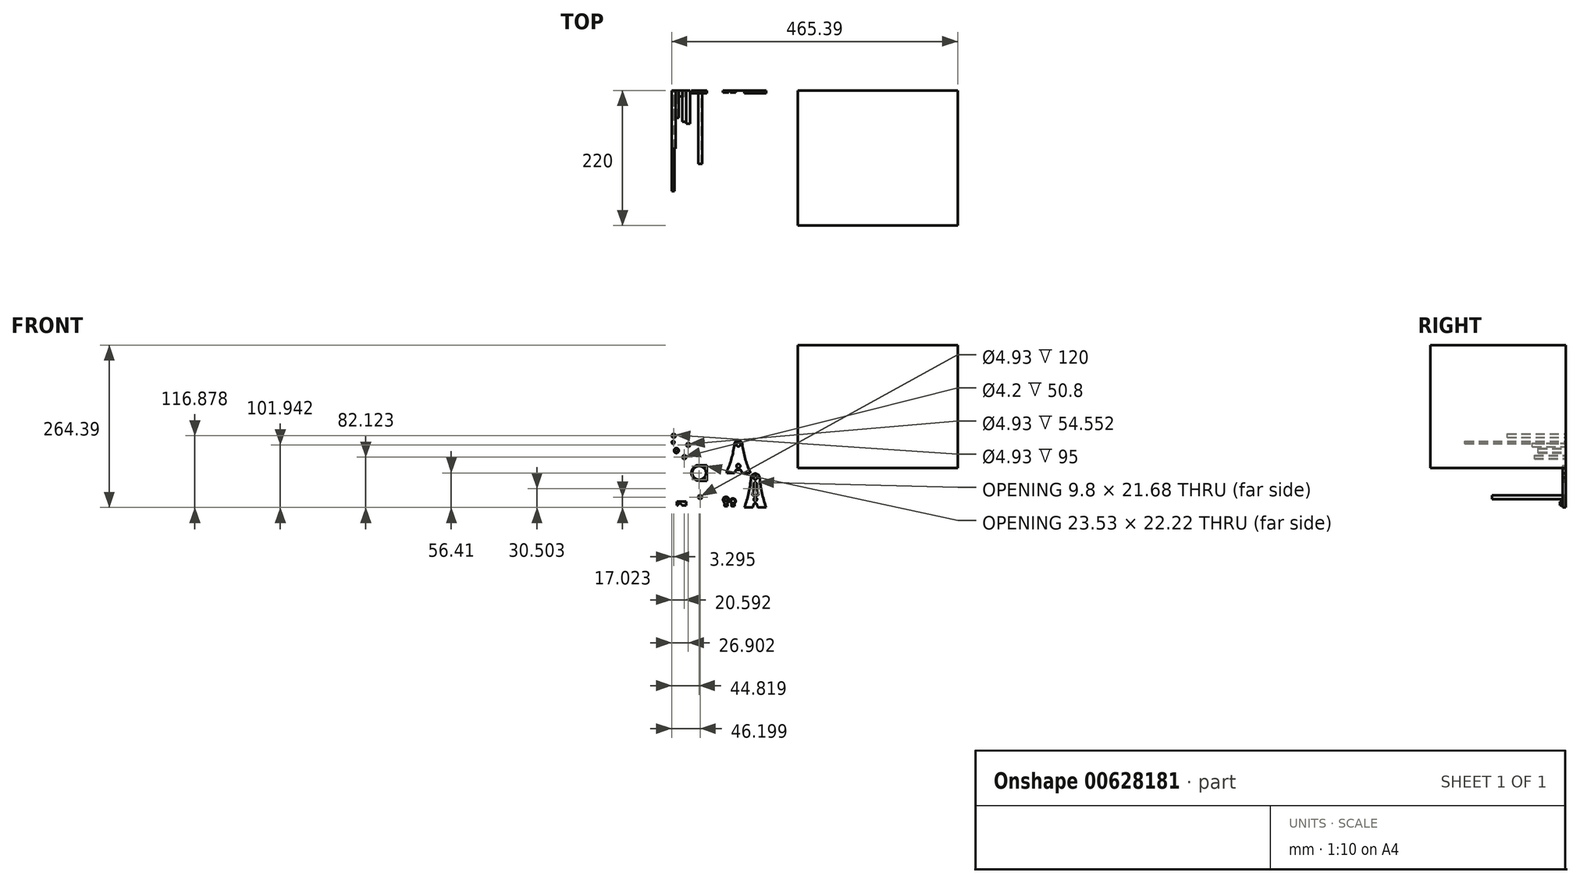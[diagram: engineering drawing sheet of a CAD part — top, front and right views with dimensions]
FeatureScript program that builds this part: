
annotation { "Feature Type Name" : "Feature", "Feature Type Description" : "" }
export const myFeature = defineFeature(function(context is Context, id is Id, definition is map)
    precondition{}
    {
        {
            var Q0;
            Q0=qCreatedBy(makeId("Front.planeOp"),FACE);
            var sketch = newSketch(context, id + "F0", { "sketchPlane" : qUnion([Q0])});
            skLineSegment(sketch, "E0", {"start": v(35.24, 47.42) * mm, "end": v(35.24, 0) * mm, "construction": true});
            skLineSegment(sketch, "E1", {"start": v(16.19, 0) * mm, "end": v(28.89, 0) * mm});
            skCircle(sketch, "E2", {"center": v(35.24, 46.26) * mm, "radius": 3.18 * mm});
            skArc(sketch, "E3", {"start": v(41.73, 46.58) * mm, "mid": v(35.24, 52.76) * mm, "end": v(28.75, 46.58) * mm});
            skLineSegment(sketch, "E4", {"start": v(27.67, 28.76) * mm, "end": v(44.56, 28.76) * mm, "construction": true});
            skCircle(sketch, "E5.MirrorC", {"center": v(35.24, 11.26) * mm, "radius": 3.18 * mm});
            skArc(sketch, "E6.MirrorC", {"start": v(29.85, 7.62) * mm, "mid": v(36.53, 17.63) * mm, "end": v(38.78, 5.81) * mm, "construction": true});
            skLineSegment(sketch, "E7.MirrorCS", {"start": v(54.29, 0) * mm, "end": v(41.59, 0) * mm});
            skPoint(sketch, "E8.orphan", {"position": v(35.24, 0) * mm});
            skArc(sketch, "E9", {"start": v(37.6, 5.2) * mm, "mid": v(33.59, 4.98) * mm, "end": v(30.21, 7.14) * mm});
            skArc(sketch, "E10.trimOffspring", {"start": v(37.92, 5.34) * mm, "mid": v(34.3, 4.83) * mm, "end": v(31, 6.34) * mm, "construction": true});
            skPoint(sketch, "E11.visualSharp", {"position": v(30.21, 7.14) * mm});
            skPoint(sketch, "E12.visualSharp", {"position": v(38.71, 5.77) * mm});
            skLineSegment(sketch, "E13", {"start": v(41.59, 0) * mm, "end": v(39.52, 4.43) * mm});
            skArc(sketch, "E14.filletArc", {"start": v(39.52, 4.43) * mm, "mid": v(38.71, 5.2) * mm, "end": v(37.6, 5.2) * mm});
            skArc(sketch, "E15.MirrorCS", {"start": v(30.95, 4.43) * mm, "mid": v(31.77, 5.2) * mm, "end": v(32.89, 5.2) * mm});
            skLineSegment(sketch, "E16.MirrorCS", {"start": v(28.89, 0) * mm, "end": v(30.95, 4.43) * mm});
            skArc(sketch, "E17", {"start": v(35.17, 39.95) * mm, "mid": v(35.24, 39.95) * mm, "end": v(35.3, 39.95) * mm});
            skArc(sketch, "E18", {"start": v(33.18, 18.44) * mm, "mid": v(35.24, 17.76) * mm, "end": v(37.3, 18.44) * mm});
            skPoint(sketch, "E19.orphan", {"position": v(42.82, 7.9) * mm});
            skPoint(sketch, "E20.orphan", {"position": v(27.65, 7.9) * mm});
            skPoint(sketch, "E21.orphan", {"position": v(35.94, 39.83) * mm});
            skPoint(sketch, "E22.orphan", {"position": v(34.54, 39.83) * mm});
            skPoint(sketch, "E23.visualSharp", {"position": v(31.8, 21.04) * mm});
            skArc(sketch, "E23.filletArc", {"start": v(32.02, 21.82) * mm, "mid": v(32.08, 19.95) * mm, "end": v(33.18, 18.44) * mm});
            skPoint(sketch, "E24.visualSharp", {"position": v(38.68, 21.04) * mm});
            skArc(sketch, "E24.filletArc", {"start": v(37.3, 18.44) * mm, "mid": v(38.4, 19.95) * mm, "end": v(38.46, 21.82) * mm});
            skLineSegment(sketch, "E25", {"start": v(16.19, 0) * mm, "end": v(16.19, 1.6) * mm});
            skArc(sketch, "E26", {"start": v(34.99, 37.23) * mm, "mid": v(35.24, 37.2) * mm, "end": v(35.5, 37.23) * mm});
            skPoint(sketch, "E26.first.point", {"position": v(35.24, 39.95) * mm});
            skArc(sketch, "E27.MirrorCS", {"start": v(54.29, 1.6) * mm, "mid": v(46.28, 23.6) * mm, "end": v(41.73, 46.58) * mm});
            skLineSegment(sketch, "E28.MirrorCS", {"start": v(54.29, 0) * mm, "end": v(54.29, 1.6) * mm});
            skLineSegment(sketch, "E29", {"start": v(28.75, 46.58) * mm, "end": v(28.75, 46.45) * mm});
            skArc(sketch, "E30", {"start": v(16.19, 1.6) * mm, "mid": v(24.2, 23.54) * mm, "end": v(28.75, 46.45) * mm});
            skSolve(sketch);
        }
        {
            var Q0;
            Q0=makeQuery(id+"F0.imprint","IMPRINT",FACE,{"disambiguationData":[TD([[makeQuery(id+"F0.imprint","IMPRINT",EDGE,{"derivedFrom":sQuery(id+"F0.wireOp",EDGE,"E1")}),1.0]])]});
            extrude(context, id + "F1", {"entities" : qUnion([Q0]), "depth" : 3 / 406.4 * mm});
        }
        {
            var Q0;
            Q0=qCreatedBy(makeId("Front.planeOp"),FACE);
            var sketch = newSketch(context, id + "F2", { "sketchPlane" : qUnion([Q0])});
            skCircle(sketch, "E31", {"center": v(-27.02, -39.39) * mm, "radius": 3.18 * mm});
            skCircle(sketch, "E32", {"center": v(-27.02, -39.39) * mm, "radius": 2.46 * mm});
            skSolve(sketch);
        }
        {
            var Q0;
            Q0=makeQuery(id+"F2.imprint","IMPRINT",FACE,{"disambiguationData":[TD([[makeQuery(id+"F2.imprint","IMPRINT",EDGE,{"derivedFrom":sQuery(id+"F2.wireOp",EDGE,"E31")}),1.0]])]});
            extrude(context, id + "F3", {"entities" : qUnion([Q0]), "depth" : 120 * mm});
        }
        {
            var Q0;
            Q0=qCreatedBy(makeId("Front.planeOp"),FACE);
            var sketch = newSketch(context, id + "F4", { "sketchPlane" : qUnion([Q0])});
            skLineSegment(sketch, "E33", {"start": v(12.66, -54.03) * mm, "end": v(12.66, -50.33) * mm});
            skLineSegment(sketch, "E34", {"start": v(17.38, -54.03) * mm, "end": v(17.38, -50.33) * mm});
            skLineSegment(sketch, "E35", {"start": v(12.66, -54.03) * mm, "end": v(17.38, -54.03) * mm});
            skLineSegment(sketch, "E36", {"start": v(17.38, -49.3) * mm, "end": v(18.1, -49.3) * mm});
            skLineSegment(sketch, "E37", {"start": v(18.1, -49.3) * mm, "end": v(18.1, -48.95) * mm});
            skLineSegment(sketch, "E38", {"start": v(15.02, -54.03) * mm, "end": v(15.02, -39.64) * mm, "construction": true});
            skLineSegment(sketch, "E39.MirrorCS", {"start": v(11.94, -49.3) * mm, "end": v(11.94, -48.95) * mm});
            skLineSegment(sketch, "E40.MirrorCS", {"start": v(12.66, -49.3) * mm, "end": v(11.94, -49.3) * mm});
            skLineSegment(sketch, "E41", {"start": v(11.94, -48.3) * mm, "end": v(18.1, -48.3) * mm, "construction": true});
            skArc(sketch, "E42", {"start": v(18.94, -46.24) * mm, "mid": v(15.02, -38.77) * mm, "end": v(11.1, -46.24) * mm});
            skCircle(sketch, "E43", {"center": v(15.02, -43.53) * mm, "radius": 2.5 * mm});
            skArc(sketch, "E44", {"start": v(18.94, -46.24) * mm, "mid": v(19.56, -44.95) * mm, "end": v(19.78, -43.53) * mm, "construction": true});
            skArc(sketch, "E45.filletArc", {"start": v(18.94, -46.24) * mm, "mid": v(18.3, -47.53) * mm, "end": v(18.1, -48.95) * mm});
            skArc(sketch, "E46.MirrorCS", {"start": v(11.1, -46.24) * mm, "mid": v(11.73, -47.53) * mm, "end": v(11.94, -48.95) * mm});
            skArc(sketch, "E47", {"start": v(11.1, -46.24) * mm, "mid": v(15.02, -48.3) * mm, "end": v(18.94, -46.24) * mm, "construction": true});
            skArc(sketch, "E48", {"start": v(17.38, -49.3) * mm, "mid": v(16.87, -49.82) * mm, "end": v(17.38, -50.33) * mm});
            skPoint(sketch, "E49.MirrorCS.start.orphan", {"position": v(18.1, -48.3) * mm});
            skPoint(sketch, "E50.MirrorCS.start.orphan", {"position": v(11.94, -48.3) * mm});
            skArc(sketch, "E51.MirrorCS", {"start": v(12.66, -49.3) * mm, "mid": v(13.16, -49.82) * mm, "end": v(12.66, -50.33) * mm});
            skPoint(sketch, "E52.orphan", {"position": v(12.66, -49.3) * mm});
            skSolve(sketch);
        }
        {
            var Q0;
            Q0=makeQuery(id+"F4.imprint","IMPRINT",FACE,{"disambiguationData":[TD([[makeQuery(id+"F4.imprint","IMPRINT",EDGE,{"derivedFrom":sQuery(id+"F4.wireOp",EDGE,"E33")}),-1.0]])]});
            extrude(context, id + "F5", {"entities" : qUnion([Q0]), "depth" : 3.17 * mm});
        }
        {
            var Q0;
            Q0=makeQuery(id+"F5.opExtrude","SWEPT_FACE",FACE,{"disambiguationData":[OSD([sQuery(id+"F4.wireOp",EDGE,"E35")])]});
            var sketch = newSketch(context, id + "F6", { "sketchPlane" : qUnion([Q0])});
            skLineSegment(sketch, "E53", {"start": v(15.02, 3.18) * mm, "end": v(15.02, 0) * mm, "construction": true});
            skLineSegment(sketch, "E54", {"start": v(12.66, 1.59) * mm, "end": v(17.38, 1.59) * mm, "construction": true});
            skCircle(sketch, "E55", {"center": v(15.02, 1.59) * mm, "radius": 2.37 * mm});
            skSolve(sketch);
        }
        {
            var Q0;
            {var subQ0=sQuery(id+"F6.wireOp",EDGE,"E55");var subQ1=sQuery(id+"F4.wireOp",EDGE,"E35");var subQ2=makeQuery(id+"F5.opExtrude","CAP_EDGE",EDGE,{"disambiguationData":[OSD([subQ1])],"isStart":false});var subQ3=makeQuery(id+"F6.imprint","INTERSECT",VERTEX,{"disambiguationData":[OD(1.0)],"derivedFrom":[subQ2,subQ0]});Q0=makeQuery(id+"F6.imprint","IMPRINT",FACE,{"disambiguationData":[TD([[makeQuery(id+"F6.imprint","IMPRINT",EDGE,{"disambiguationData":[TD([[subQ3,-1.0]])],"derivedFrom":subQ0}),-1.0]])]});}
            var Q1;
            {var subQ0=sQuery(id+"F6.wireOp",EDGE,"E55");var subQ1=sQuery(id+"F4.wireOp",EDGE,"E35");var subQ2=makeQuery(id+"F5.opExtrude","CAP_EDGE",EDGE,{"disambiguationData":[OSD([subQ1])],"isStart":false});var subQ3=makeQuery(id+"F6.imprint","INTERSECT",VERTEX,{"disambiguationData":[OD(0.0)],"derivedFrom":[subQ2,subQ0]});Q1=makeQuery(id+"F6.imprint","IMPRINT",FACE,{"disambiguationData":[TD([[makeQuery(id+"F6.imprint","IMPRINT",EDGE,{"disambiguationData":[TD([[subQ3,1.0]])],"derivedFrom":subQ0}),-1.0]])]});}
            var Q2;
            {var subQ0=sQuery(id+"F6.wireOp",EDGE,"E55");var subQ1=sQuery(id+"F4.wireOp",EDGE,"E35");var subQ4=makeQuery(id+"F5.opExtrude","CAP_EDGE",EDGE,{"disambiguationData":[OSD([subQ1])],"isStart":true});var subQ5=makeQuery(id+"F6.imprint","INTERSECT",VERTEX,{"disambiguationData":[OD(1.0)],"derivedFrom":[subQ4,subQ0]});Q2=makeQuery(id+"F6.imprint","IMPRINT",FACE,{"disambiguationData":[TD([[makeQuery(id+"F6.imprint","IMPRINT",EDGE,{"disambiguationData":[TD([[subQ5,-1.0]])],"derivedFrom":subQ0}),-1.0]])]});}
            var Q3;
            {var subQ0=sQuery(id+"F6.wireOp",EDGE,"E55");var subQ1=sQuery(id+"F4.wireOp",EDGE,"E35");var subQ4=makeQuery(id+"F5.opExtrude","CAP_EDGE",EDGE,{"disambiguationData":[OSD([subQ1])],"isStart":true});var subQ5=makeQuery(id+"F6.imprint","INTERSECT",VERTEX,{"disambiguationData":[OD(0.0)],"derivedFrom":[subQ4,subQ0]});Q3=makeQuery(id+"F6.imprint","IMPRINT",FACE,{"disambiguationData":[TD([[makeQuery(id+"F6.imprint","IMPRINT",EDGE,{"disambiguationData":[TD([[subQ5,1.0]])],"derivedFrom":subQ0}),-1.0]])]});}
            var Q4;
            Q4=sQuery(id+"F6.wireOp",EDGE,"E55");
            var Q5;
            Q5=makeQuery(id+"F5.opExtrude","SWEPT_FACE",FACE,{"disambiguationData":[OSD([sQuery(id+"F4.wireOp",EDGE,"E40.MirrorCS")])]});
            extrude(context, id + "F7", {"entities" : qUnion([Q0, Q1, Q2, Q3]), "operationType" : NewBodyOperationType.REMOVE, "surfaceEntities" : qUnion([Q4]), "endBound" : BoundingType.UP_TO_SURFACE, "oppositeDirection" : true, "endBoundEntityFace" : qUnion([Q5]), "depth" : 25.4 * mm});
        }
        {
            var Q0;
            Q0=qCreatedBy(makeId("Front.planeOp"),FACE);
            var sketch = newSketch(context, id + "F8", { "sketchPlane" : qUnion([Q0])});
            skLineSegment(sketch, "E56", {"start": v(24.01, -54.08) * mm, "end": v(28.94, -54.08) * mm});
            skLineSegment(sketch, "E57", {"start": v(28.94, -54.08) * mm, "end": v(28.94, -50.16) * mm});
            skLineSegment(sketch, "E58", {"start": v(24.01, -54.08) * mm, "end": v(24.01, -50.16) * mm});
            skArc(sketch, "E59", {"start": v(28.94, -49.15) * mm, "mid": v(28.43, -49.66) * mm, "end": v(28.94, -50.16) * mm});
            skLineSegment(sketch, "E60", {"start": v(26.48, -54.08) * mm, "end": v(26.48, -44.7) * mm, "construction": true});
            skLineSegment(sketch, "E61", {"start": v(28.94, -49.15) * mm, "end": v(29.65, -49.15) * mm});
            skLineSegment(sketch, "E62", {"start": v(28.94, -49.15) * mm, "end": v(26.48, -49.15) * mm, "construction": true});
            skArc(sketch, "E63.MirrorCS", {"start": v(24.01, -49.15) * mm, "mid": v(24.52, -49.66) * mm, "end": v(24.01, -50.16) * mm});
            skLineSegment(sketch, "E64.MirrorCS", {"start": v(24.01, -49.15) * mm, "end": v(23.3, -49.15) * mm});
            skCircle(sketch, "E65", {"center": v(26.48, -45.97) * mm, "radius": 3.18 * mm});
            skArc(sketch, "E66", {"start": v(29.65, -49.15) * mm, "mid": v(26.48, -41.48) * mm, "end": v(23.3, -49.15) * mm});
            skSolve(sketch);
        }
        {
            var Q0;
            Q0=makeQuery(id+"F8.imprint","IMPRINT",FACE,{"disambiguationData":[TD([[makeQuery(id+"F8.imprint","IMPRINT",EDGE,{"derivedFrom":sQuery(id+"F8.wireOp",EDGE,"E56")}),1.0]])]});
            extrude(context, id + "F9", {"entities" : qUnion([Q0]), "depth" : 3.17 * mm});
        }
        {
            var Q0;
            Q0=makeQuery(id+"F9.opExtrude","SWEPT_FACE",FACE,{"disambiguationData":[OSD([sQuery(id+"F8.wireOp",EDGE,"E56")])]});
            var sketch = newSketch(context, id + "F10", { "sketchPlane" : qUnion([Q0])});
            skLineSegment(sketch, "E67", {"start": v(28.94, 1.59) * mm, "end": v(24.01, 1.59) * mm, "construction": true});
            skLineSegment(sketch, "E68", {"start": v(26.48, 3.01) * mm, "end": v(26.48, 0) * mm, "construction": true});
            skPoint(sketch, "E68.startSnap0", {"position": v(26.48, 3.18) * mm});
            skCircle(sketch, "E69", {"center": v(26.48, 1.59) * mm, "radius": 2.46 * mm});
            skSolve(sketch);
        }
        {
            var Q0;
            {var subQ0=sQuery(id+"F10.wireOp",EDGE,"E69");var subQ1=sQuery(id+"F8.wireOp",EDGE,"E56");var subQ2=makeQuery(id+"F9.opExtrude","CAP_EDGE",EDGE,{"disambiguationData":[OSD([subQ1])],"isStart":false});var subQ3=makeQuery(id+"F10.imprint","INTERSECT",VERTEX,{"disambiguationData":[OD(1.0)],"derivedFrom":[subQ2,subQ0]});Q0=makeQuery(id+"F10.imprint","IMPRINT",FACE,{"disambiguationData":[TD([[makeQuery(id+"F10.imprint","IMPRINT",EDGE,{"disambiguationData":[TD([[subQ3,-1.0]])],"derivedFrom":subQ0}),-1.0]])]});}
            var Q1;
            {var subQ0=sQuery(id+"F10.wireOp",EDGE,"E69");var subQ1=sQuery(id+"F8.wireOp",EDGE,"E56");var subQ2=makeQuery(id+"F9.opExtrude","CAP_EDGE",EDGE,{"disambiguationData":[OSD([subQ1])],"isStart":false});var subQ3=makeQuery(id+"F10.imprint","INTERSECT",VERTEX,{"disambiguationData":[OD(0.0)],"derivedFrom":[subQ2,subQ0]});Q1=makeQuery(id+"F10.imprint","IMPRINT",FACE,{"disambiguationData":[TD([[makeQuery(id+"F10.imprint","IMPRINT",EDGE,{"disambiguationData":[TD([[subQ3,1.0]])],"derivedFrom":subQ0}),-1.0]])]});}
            var Q2;
            {var subQ0=sQuery(id+"F10.wireOp",EDGE,"E69");var subQ1=sQuery(id+"F8.wireOp",EDGE,"E56");var subQ4=makeQuery(id+"F9.opExtrude","CAP_EDGE",EDGE,{"disambiguationData":[OSD([subQ1])],"isStart":true});var subQ5=makeQuery(id+"F10.imprint","INTERSECT",VERTEX,{"disambiguationData":[OD(0.0)],"derivedFrom":[subQ4,subQ0]});Q2=makeQuery(id+"F10.imprint","IMPRINT",FACE,{"disambiguationData":[TD([[makeQuery(id+"F10.imprint","IMPRINT",EDGE,{"disambiguationData":[TD([[subQ5,1.0]])],"derivedFrom":subQ0}),-1.0]])]});}
            var Q3;
            {var subQ0=sQuery(id+"F10.wireOp",EDGE,"E69");var subQ1=sQuery(id+"F8.wireOp",EDGE,"E56");var subQ4=makeQuery(id+"F9.opExtrude","CAP_EDGE",EDGE,{"disambiguationData":[OSD([subQ1])],"isStart":true});var subQ5=makeQuery(id+"F10.imprint","INTERSECT",VERTEX,{"disambiguationData":[OD(1.0)],"derivedFrom":[subQ4,subQ0]});Q3=makeQuery(id+"F10.imprint","IMPRINT",FACE,{"disambiguationData":[TD([[makeQuery(id+"F10.imprint","IMPRINT",EDGE,{"disambiguationData":[TD([[subQ5,-1.0]])],"derivedFrom":subQ0}),-1.0]])]});}
            var Q4;
            Q4=makeQuery(id+"F9.opExtrude","SWEPT_FACE",FACE,{"disambiguationData":[OSD([sQuery(id+"F8.wireOp",EDGE,"E64.MirrorCS")])]});
            extrude(context, id + "F11", {"entities" : qUnion([Q0, Q1, Q2, Q3]), "operationType" : NewBodyOperationType.REMOVE, "endBound" : BoundingType.UP_TO_SURFACE, "oppositeDirection" : true, "endBoundEntityFace" : qUnion([Q4]), "depth" : 25.4 * mm});
        }
        {
            var Q0;
            Q0=qCreatedBy(makeId("Front.planeOp"),FACE);
            var sketch = newSketch(context, id + "F12", { "sketchPlane" : qUnion([Q0])});
            skLineSegment(sketch, "E70", {"start": v(45.19, -56.41) * mm, "end": v(58.6, -56.41) * mm});
            skLineSegment(sketch, "E71", {"start": v(62.84, -56.41) * mm, "end": v(62.84, 31.77) * mm, "construction": true});
            skCircle(sketch, "E72", {"center": v(62.84, -43.06) * mm, "radius": 7 * mm, "construction": true});
            skCircle(sketch, "E73", {"center": v(62.84, -43.06) * mm, "radius": 2.87 * mm});
            skCircle(sketch, "E74", {"center": v(62.84, -8.06) * mm, "radius": 7 * mm, "construction": true});
            skCircle(sketch, "E75", {"center": v(62.84, -8.06) * mm, "radius": 2.87 * mm});
            skLineSegment(sketch, "E76", {"start": v(62.84, -8.06) * mm, "end": v(55.84, -8.06) * mm, "construction": true});
            skArc(sketch, "E77", {"start": v(45.19, -56.41) * mm, "mid": v(52, -32.57) * mm, "end": v(55.84, -8.06) * mm});
            skArc(sketch, "E78", {"start": v(69.84, -8.06) * mm, "mid": v(62.84, -1.06) * mm, "end": v(55.84, -8.06) * mm});
            skArc(sketch, "E79.0", {"start": v(57.98, -34.9) * mm, "mid": v(59.84, -25.68) * mm, "end": v(61.28, -16.39) * mm});
            skArc(sketch, "E80.0", {"start": v(58.6, -56.41) * mm, "mid": v(59.46, -53.75) * mm, "end": v(60.29, -51.08) * mm});
            skArc(sketch, "E81", {"start": v(62.8, -15.06) * mm, "mid": v(62.82, -15.06) * mm, "end": v(62.84, -15.06) * mm});
            skArc(sketch, "E82", {"start": v(60.07, -36.64) * mm, "mid": v(61.43, -36.2) * mm, "end": v(62.84, -36.06) * mm});
            skArc(sketch, "E83", {"start": v(61.94, -50) * mm, "mid": v(62.4, -50.05) * mm, "end": v(62.84, -50.06) * mm});
            skPoint(sketch, "E84.visualSharp", {"position": v(56.94, -39.3) * mm});
            skArc(sketch, "E84.filletArc", {"start": v(57.98, -34.9) * mm, "mid": v(58.5, -36.41) * mm, "end": v(60.07, -36.64) * mm});
            skPoint(sketch, "E85.visualSharp", {"position": v(60.7, -49.73) * mm});
            skArc(sketch, "E85.filletArc", {"start": v(61.94, -50) * mm, "mid": v(60.92, -50.24) * mm, "end": v(60.29, -51.08) * mm});
            skPoint(sketch, "E86.visualSharp", {"position": v(61.47, -14.93) * mm});
            skArc(sketch, "E86.filletArc", {"start": v(62.8, -15.06) * mm, "mid": v(61.8, -15.44) * mm, "end": v(61.28, -16.39) * mm});
            skArc(sketch, "E87.MirrorCS", {"start": v(67.7, -34.9) * mm, "mid": v(65.84, -25.68) * mm, "end": v(64.4, -16.39) * mm});
            skPoint(sketch, "E88.MirrorP", {"position": v(64.21, -14.93) * mm});
            skArc(sketch, "E89.MirrorCS", {"start": v(62.88, -15.06) * mm, "mid": v(63.89, -15.44) * mm, "end": v(64.4, -16.39) * mm});
            skArc(sketch, "E90.MirrorCS", {"start": v(67.7, -34.9) * mm, "mid": v(67.2, -36.41) * mm, "end": v(65.62, -36.64) * mm});
            skArc(sketch, "E91.MirrorCS", {"start": v(63.74, -50) * mm, "mid": v(64.76, -50.24) * mm, "end": v(65.4, -51.08) * mm});
            skArc(sketch, "E92.MirrorCS", {"start": v(67.08, -56.41) * mm, "mid": v(66.22, -53.75) * mm, "end": v(65.4, -51.08) * mm});
            skLineSegment(sketch, "E93.MirrorCS", {"start": v(80.5, -56.41) * mm, "end": v(67.08, -56.41) * mm});
            skArc(sketch, "E94.MirrorCS", {"start": v(80.5, -56.41) * mm, "mid": v(73.7, -32.57) * mm, "end": v(69.84, -8.06) * mm});
            skPoint(sketch, "E95.orphan", {"position": v(62.84, -56.41) * mm});
            skArc(sketch, "E96", {"start": v(62.84, -36.06) * mm, "mid": v(64.26, -36.2) * mm, "end": v(65.62, -36.64) * mm});
            skArc(sketch, "E97", {"start": v(62.84, -50.06) * mm, "mid": v(63.3, -50.05) * mm, "end": v(63.74, -50) * mm});
            skArc(sketch, "E98.MirrorCS", {"start": v(62.88, -15.06) * mm, "mid": v(62.86, -15.06) * mm, "end": v(62.84, -15.06) * mm});
            skSolve(sketch);
        }
        {
            var Q0;
            Q0=makeQuery(id+"F12.imprint","IMPRINT",FACE,{"disambiguationData":[TD([[makeQuery(id+"F12.imprint","IMPRINT",EDGE,{"derivedFrom":sQuery(id+"F12.wireOp",EDGE,"E70")}),1.0]])]});
            extrude(context, id + "F13", {"entities" : qUnion([Q0]), "depth" : 4.76 * mm});
        }
        {
            var Q0;
            Q0=qCreatedBy(makeId("Front.planeOp"),FACE);
            var sketch = newSketch(context, id + "F14", { "sketchPlane" : qUnion([Q0])});
            skLineSegment(sketch, "E99", {"start": v(-64.6, -53.03) * mm, "end": v(-64.6, -46.68) * mm});
            skLineSegment(sketch, "E100", {"start": v(-64.6, -46.68) * mm, "end": v(-54.3, -46.68) * mm});
            skLineSegment(sketch, "E101", {"start": v(-49.54, -46.68) * mm, "end": v(-49.54, -53.03) * mm});
            skLineSegment(sketch, "E102", {"start": v(-49.54, -53.03) * mm, "end": v(-56.65, -53.03) * mm});
            skLineSegment(sketch, "E103", {"start": v(-63, -53.03) * mm, "end": v(-64.6, -53.03) * mm});
            skLineSegment(sketch, "E104", {"start": v(-56.27, -46.68) * mm, "end": v(-56.27, -53.03) * mm, "construction": true});
            skLineSegment(sketch, "E105", {"start": v(-49.92, -46.68) * mm, "end": v(-49.92, -53.03) * mm, "construction": true});
            skLineSegment(sketch, "E106", {"start": v(-56.27, -46.98) * mm, "end": v(-49.92, -46.98) * mm, "construction": true});
            skLineSegment(sketch, "E107", {"start": v(-52.74, -46.83) * mm, "end": v(-52.59, -46.68) * mm});
            skPoint(sketch, "E107.startSnap0", {"position": v(-53.1, -46.98) * mm});
            skLineSegment(sketch, "E108", {"start": v(-53.45, -46.83) * mm, "end": v(-53.6, -46.68) * mm});
            skPoint(sketch, "E109.visualSharp", {"position": v(-53.1, -47.19) * mm});
            skArc(sketch, "E109.filletArc", {"start": v(-53.45, -46.83) * mm, "mid": v(-53.1, -46.98) * mm, "end": v(-52.74, -46.83) * mm});
            skArc(sketch, "E110", {"start": v(-56.65, -53.03) * mm, "mid": v(-59.83, -49.85) * mm, "end": v(-63, -53.03) * mm});
            skLineSegment(sketch, "E111", {"start": v(-53.1, -53.03) * mm, "end": v(-53.1, -46.68) * mm, "construction": true});
            skLineSegment(sketch, "E112", {"start": v(-54.3, -46.68) * mm, "end": v(-53.6, -46.68) * mm});
            skLineSegment(sketch, "E113", {"start": v(-49.92, -46.68) * mm, "end": v(-52.59, -46.68) * mm});
            skLineSegment(sketch, "E114", {"start": v(-49.54, -46.68) * mm, "end": v(-49.92, -46.68) * mm});
            skSolve(sketch);
        }
        {
            var Q0;
            Q0=qSketchRegion(id+"F14",true);
            extrude(context, id + "F15", {"entities" : qUnion([Q0]), "depth" : 9.52 * mm});
        }
        {
            var Q0;
            Q0=qCreatedBy(makeId("Front.planeOp"),FACE);
            var sketch = newSketch(context, id + "F16", { "sketchPlane" : qUnion([Q0])});
            skCircle(sketch, "E115", {"center": v(-46.32, 45.53) * mm, "radius": 3.18 * mm});
            skCircle(sketch, "E116", {"center": v(-46.32, 45.53) * mm, "radius": 2.46 * mm});
            skSolve(sketch);
        }
        {
            var Q0;
            Q0=makeQuery(id+"F16.imprint","IMPRINT",FACE,{"disambiguationData":[TD([[makeQuery(id+"F16.imprint","IMPRINT",EDGE,{"derivedFrom":sQuery(id+"F16.wireOp",EDGE,"E115")}),1.0]])]});
            extrude(context, id + "F17", {"entities" : qUnion([Q0]), "depth" : 54.55 * mm});
        }
        {
            var Q0;
            Q0=qCreatedBy(makeId("Front.planeOp"),FACE);
            var sketch = newSketch(context, id + "F18", { "sketchPlane" : qUnion([Q0])});
            skCircle(sketch, "E117", {"center": v(-52.63, 25.71) * mm, "radius": 3.18 * mm});
            skCircle(sketch, "E118", {"center": v(-52.63, 25.71) * mm, "radius": 2.1 * mm});
            skSolve(sketch);
        }
        {
            var Q0;
            Q0=makeQuery(id+"F18.imprint","IMPRINT",FACE,{"disambiguationData":[TD([[makeQuery(id+"F18.imprint","IMPRINT",EDGE,{"derivedFrom":sQuery(id+"F18.wireOp",EDGE,"E117")}),1.0]])]});
            extrude(context, id + "F19", {"entities" : qUnion([Q0]), "depth" : 50.8 * mm});
        }
        {
            var Q0;
            Q0=qCreatedBy(makeId("Front.planeOp"),FACE);
            var sketch = newSketch(context, id + "F20", { "sketchPlane" : qUnion([Q0])});
            skLineSegment(sketch, "E119.0", {"start": v(-8.85, -6.35) * mm, "end": v(-8.85, 0) * mm});
            skLineSegment(sketch, "E120.0", {"start": v(-34.27, -6.35) * mm, "end": v(-8.85, -6.35) * mm});
            skLineSegment(sketch, "E121.0", {"start": v(-34.27, 0) * mm, "end": v(-8.85, 0) * mm});
            skCircle(sketch, "E122", {"center": v(-8.85, -3.18) * mm, "radius": 3.17 * mm});
            skSolve(sketch);
        }
        {
            var Q0;
            Q0=qSketchRegion(id+"F20",true);
            extrude(context, id + "F21", {"entities" : qUnion([Q0]), "operationType" : NewBodyOperationType.REMOVE, "endBound" : BoundingType.SYMMETRIC, "oppositeDirection" : true, "depth" : 25.4 * mm});
        }
        {
            var Q0;
            Q0=qCreatedBy(makeId("Front.planeOp"),FACE);
            var sketch = newSketch(context, id + "F22", { "sketchPlane" : qUnion([Q0])});
            skArc(sketch, "E123", {"start": v(-39.65, -0.5) * mm, "mid": v(-28.7, -11.11) * mm, "end": v(-17.46, -0.8) * mm});
            skArc(sketch, "E124", {"start": v(-28.55, 12.7) * mm, "mid": v(-41.25, 0) * mm, "end": v(-28.55, -12.7) * mm});
            skLineSegment(sketch, "E125", {"start": v(-41.25, 0) * mm, "end": v(-15.85, 0) * mm, "construction": true});
            skLineSegment(sketch, "E126", {"start": v(-15.85, -22.43) * mm, "end": v(-15.85, 22.43) * mm, "construction": true});
            skLineSegment(sketch, "E127", {"start": v(-15.85, 22.44) * mm, "end": v(-5.85, 22.44) * mm, "construction": true});
            skLineSegment(sketch, "E128", {"start": v(-5.85, 22.44) * mm, "end": v(-5.85, -22.43) * mm, "construction": true});
            skLineSegment(sketch, "E129", {"start": v(-5.85, -22.43) * mm, "end": v(-15.85, -22.43) * mm, "construction": true});
            skLineSegment(sketch, "E130", {"start": v(-15.85, 12.7) * mm, "end": v(-28.55, 12.7) * mm});
            skLineSegment(sketch, "E131.0", {"start": v(-17.12, 11.94) * mm, "end": v(-21.93, 11.94) * mm});
            skLineSegment(sketch, "E132.trimOffspring", {"start": v(-16.6, 6.62) * mm, "end": v(-16.6, 11.43) * mm});
            skPoint(sketch, "E133.visualSharp", {"position": v(-16.6, 11.94) * mm});
            skArc(sketch, "E133.filletArc", {"start": v(-16.6, 11.43) * mm, "mid": v(-16.76, 11.79) * mm, "end": v(-17.12, 11.94) * mm});
            skPoint(sketch, "E134.visualSharp", {"position": v(-23.57, 11.94) * mm});
            skArc(sketch, "E134.filletArc", {"start": v(-21.93, 11.94) * mm, "mid": v(-22.42, 11.56) * mm, "end": v(-22.18, 11) * mm});
            skPoint(sketch, "E135.visualSharp", {"position": v(-16.6, 4.98) * mm});
            skArc(sketch, "E135.filletArc", {"start": v(-17.56, 6.36) * mm, "mid": v(-16.98, 6.13) * mm, "end": v(-16.6, 6.62) * mm});
            skLineSegment(sketch, "E136.MirrorCS", {"start": v(-15.85, -12.7) * mm, "end": v(-28.55, -12.7) * mm});
            skLineSegment(sketch, "E137.MirrorCS", {"start": v(-17.12, -11.94) * mm, "end": v(-21.93, -11.94) * mm});
            skArc(sketch, "E138.MirrorCS", {"start": v(-16.6, -11.43) * mm, "mid": v(-16.76, -11.79) * mm, "end": v(-17.12, -11.94) * mm});
            skLineSegment(sketch, "E139.MirrorCS", {"start": v(-16.6, -6.62) * mm, "end": v(-16.6, -11.43) * mm});
            skArc(sketch, "E140.MirrorCS", {"start": v(-17.56, -6.36) * mm, "mid": v(-16.98, -6.13) * mm, "end": v(-16.6, -6.62) * mm});
            skArc(sketch, "E141.MirrorCS", {"start": v(-17.56, -6.36) * mm, "mid": v(-19.57, -8.98) * mm, "end": v(-22.18, -11) * mm});
            skArc(sketch, "E142.MirrorCS", {"start": v(-21.93, -11.94) * mm, "mid": v(-22.42, -11.56) * mm, "end": v(-22.18, -11) * mm});
            skArc(sketch, "E143.trimOffspring", {"start": v(-22.18, -11) * mm, "mid": v(-19.57, -8.98) * mm, "end": v(-17.56, -6.36) * mm});
            skLineSegment(sketch, "E144", {"start": v(-15.85, 12.7) * mm, "end": v(-15.85, -12.7) * mm});
            skArc(sketch, "E145", {"start": v(-39.65, 0.5) * mm, "mid": v(-40.17, 0) * mm, "end": v(-39.65, -0.5) * mm});
            skArc(sketch, "E146", {"start": v(-17.46, -0.8) * mm, "mid": v(-16.63, 0) * mm, "end": v(-17.46, 0.8) * mm});
            skArc(sketch, "E147.trimOffspring", {"start": v(-17.46, 0.8) * mm, "mid": v(-28.7, 11.11) * mm, "end": v(-39.65, 0.5) * mm});
            skArc(sketch, "E148", {"start": v(-22.18, 11) * mm, "mid": v(-19.57, 8.98) * mm, "end": v(-17.56, 6.36) * mm});
            skSolve(sketch);
        }
        {
            var Q0;
            Q0=makeQuery(id+"F22.imprint","IMPRINT",FACE,{"disambiguationData":[TD([[makeQuery(id+"F22.imprint","IMPRINT",EDGE,{"derivedFrom":sQuery(id+"F22.wireOp",EDGE,"E123")}),-1.0]])]});
            extrude(context, id + "F23", {"entities" : qUnion([Q0]), "depth" : 4.76 * mm});
        }
        {
            var Q0;
            Q0=qCreatedBy(makeId("Front.planeOp"),FACE);
            var sketch = newSketch(context, id + "F24", { "sketchPlane" : qUnion([Q0])});
            skCircle(sketch, "E149", {"center": v(-65.54, 36.33) * mm, "radius": 4 * mm});
            skCircle(sketch, "E150", {"center": v(-65.54, 36.33) * mm, "radius": 2.5 * mm});
            skSolve(sketch);
        }
        {
            var Q0;
            Q0=makeQuery(id+"F24.imprint","IMPRINT",FACE,{"disambiguationData":[TD([[makeQuery(id+"F24.imprint","IMPRINT",EDGE,{"derivedFrom":sQuery(id+"F24.wireOp",EDGE,"E149")}),1.0]])]});
            extrude(context, id + "F25", {"entities" : qUnion([Q0]), "depth" : 45 * mm});
        }
        {
            var Q0;
            Q0=qCreatedBy(makeId("Front.planeOp"),FACE);
            var sketch = newSketch(context, id + "F26", { "sketchPlane" : qUnion([Q0])});
            skLineSegment(sketch, "E151.bottom", {"start": v(132.17, 7.98) * mm, "end": v(392.17, 7.98) * mm});
            skLineSegment(sketch, "E151.top", {"start": v(132.17, 207.98) * mm, "end": v(392.17, 207.98) * mm});
            skLineSegment(sketch, "E151.left", {"start": v(132.17, 7.98) * mm, "end": v(132.17, 207.98) * mm});
            skLineSegment(sketch, "E151.right", {"start": v(392.17, 7.98) * mm, "end": v(392.17, 207.98) * mm});
            skSolve(sketch);
        }
        {
            var Q0;
            Q0=makeQuery(id+"F26.imprint","IMPRINT",FACE,{"disambiguationData":[TD([[makeQuery(id+"F26.imprint","IMPRINT",EDGE,{"derivedFrom":sQuery(id+"F26.wireOp",EDGE,"E151.bottom")}),1.0]])]});
            extrude(context, id + "F27", {"entities" : qUnion([Q0]), "depth" : 220 * mm});
        }
        {
            var Q0;
            Q0=qCreatedBy(makeId("Front.planeOp"),FACE);
            var sketch = newSketch(context, id + "F28", { "sketchPlane" : qUnion([Q0])});
            skCircle(sketch, "E152", {"center": v(-69.93, 60.47) * mm, "radius": 3.18 * mm});
            skCircle(sketch, "E153", {"center": v(-69.93, 60.47) * mm, "radius": 2.46 * mm});
            skSolve(sketch);
        }
        {
            var Q0;
            Q0=makeQuery(id+"F28.imprint","IMPRINT",FACE,{"disambiguationData":[TD([[makeQuery(id+"F28.imprint","IMPRINT",EDGE,{"derivedFrom":sQuery(id+"F28.wireOp",EDGE,"E152")}),1.0]])]});
            extrude(context, id + "F29", {"entities" : qUnion([Q0]), "depth" : 95 * mm});
        }
        {
            var Q0;
            Q0=qCreatedBy(makeId("Front.planeOp"),FACE);
            var sketch = newSketch(context, id + "F30", { "sketchPlane" : qUnion([Q0])});
            skCircle(sketch, "E154", {"center": v(-70.84, 49.64) * mm, "radius": 1.14 * mm});
            skCircle(sketch, "E155", {"center": v(-70.84, 49.64) * mm, "radius": 2.38 * mm});
            skSolve(sketch);
        }
        {
            var Q0;
            Q0=makeQuery(id+"F30.imprint","IMPRINT",FACE,{"disambiguationData":[TD([[makeQuery(id+"F30.imprint","IMPRINT",EDGE,{"derivedFrom":sQuery(id+"F30.wireOp",EDGE,"E154")}),-1.0]])]});
            extrude(context, id + "F31", {"entities" : qUnion([Q0]), "depth" : 164.24 * mm});
        }
    });
